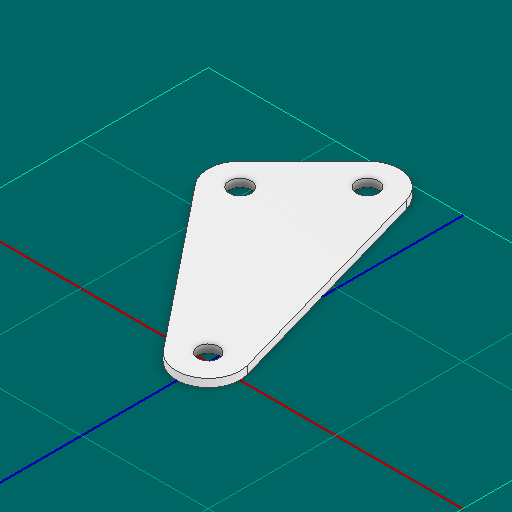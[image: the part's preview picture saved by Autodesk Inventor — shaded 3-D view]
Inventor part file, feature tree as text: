
AUTODESK INVENTOR PART (.ipt)
format: ipt  version: 2025 (Build 290162000, 162)  size: 109,568 bytes
history: native  units: in
note: dims shown in document units (in); Inventor stores cm internally (conversion verified against a paired STEP export)
features: other x3, extrude x1, sketch x1
ambient origin geometry x8: Origin, YZ Plane, XZ Plane, XY Plane, X Axis, Y Axis, Z Axis, Center Point
bodies: Solid1 (feature_tree)
feature tree (5):
  other  "Blocks"
  extrude  "Extrusion1"  Depth=0.0625in
  sketch  "Sketch1"  dims[d0=0.5in d1=0.5in d2=0.0625in d3=0.0in]
  other  "main"
  other  "main:1"
